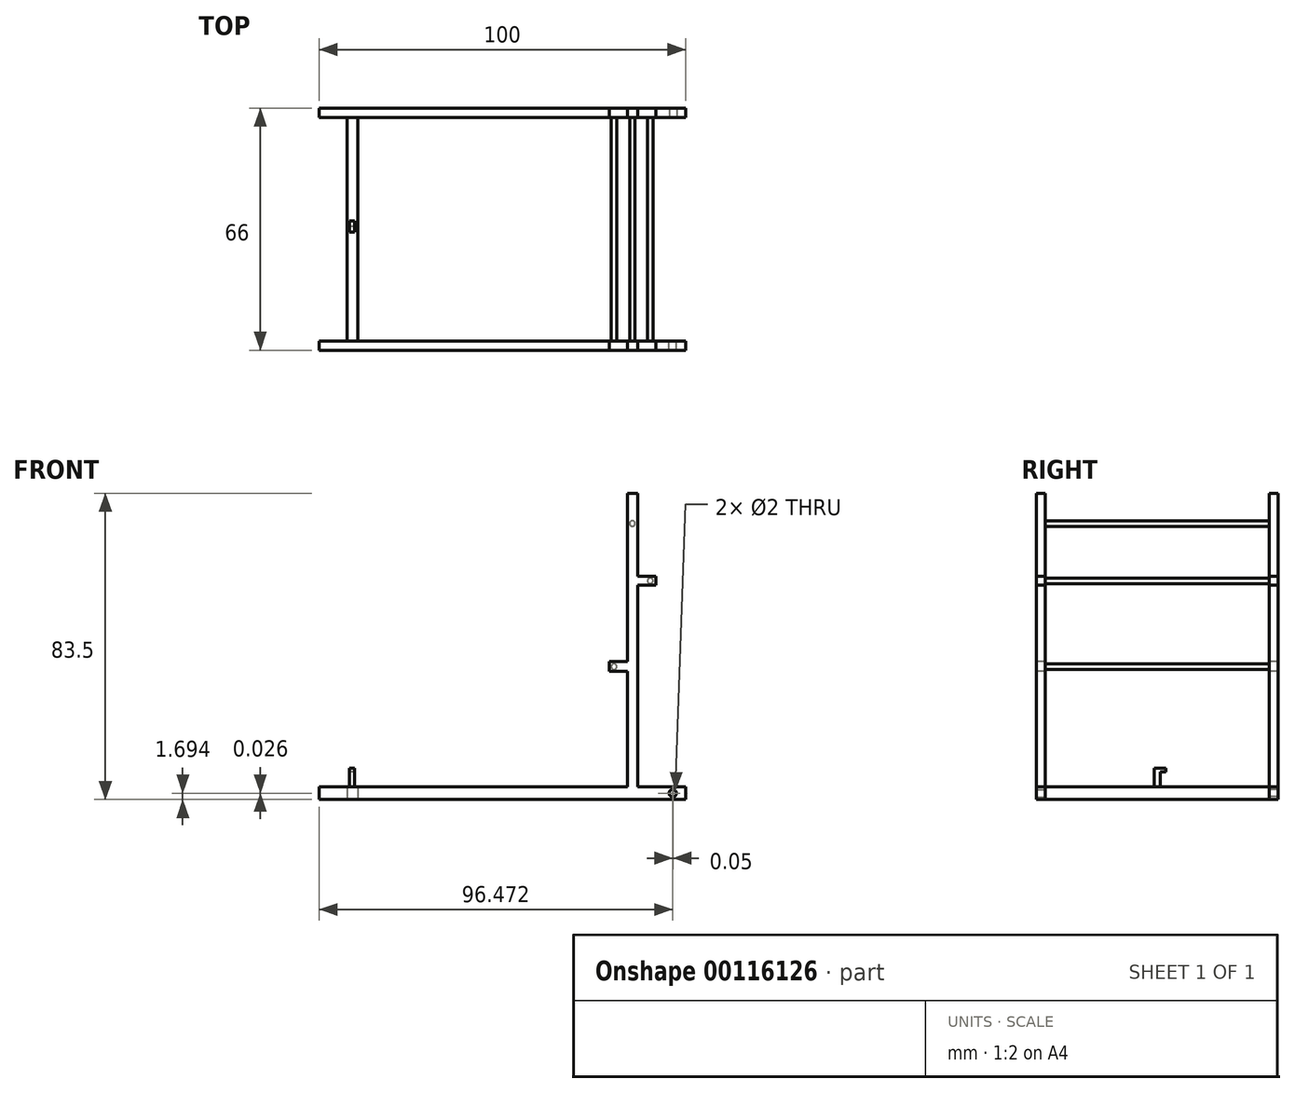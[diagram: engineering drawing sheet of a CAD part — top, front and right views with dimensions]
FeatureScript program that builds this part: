
annotation { "Feature Type Name" : "Feature", "Feature Type Description" : "" }
export const myFeature = defineFeature(function(context is Context, id is Id, definition is map)
    precondition{}
    {
        {
            var Q0;
            Q0=qCreatedBy(makeId("Front.planeOp"),FACE);
            var sketch = newSketch(context, id + "F0", { "sketchPlane" : qUnion([Q0])});
            skLineSegment(sketch, "E0", {"start": v(-48.3, 0) * mm, "end": v(51.7, 0) * mm});
            skLineSegment(sketch, "E1", {"start": v(-48.3, 0) * mm, "end": v(-48.3, 3.5) * mm});
            skLineSegment(sketch, "E2", {"start": v(-48.3, 3.5) * mm, "end": v(51.7, 3.5) * mm});
            skLineSegment(sketch, "E3", {"start": v(51.7, 3.5) * mm, "end": v(51.7, 0) * mm});
            skCircle(sketch, "E4", {"center": v(48.16, 1.7) * mm, "radius": 1 * mm});
            skSolve(sketch);
        }
        {
            var Q0;
            Q0=makeQuery(id+"F0.imprint","IMPRINT",FACE,{"disambiguationData":[TD([[makeQuery(id+"F0.imprint","IMPRINT",EDGE,{"derivedFrom":sQuery(id+"F0.wireOp",EDGE,"E0")}),1.0]])]});
            extrude(context, id + "F1", {"entities" : qUnion([Q0]), "depth" : 2.5 * mm});
        }
        {
            var Q0;
            Q0=qCreatedBy(makeId("Top.planeOp"),FACE);
            var sketch = newSketch(context, id + "F2", { "sketchPlane" : qUnion([Q0])});
            skLineSegment(sketch, "E5", {"start": v(0, 0) * mm, "end": v(0, 61) * mm});
            skSolve(sketch);
        }
        {
            var Q0;
            Q0=sQuery(id+"F2.wireOp",VERTEX,"E5.end");
            var Q1;
            Q1=qCreatedBy(makeId("Front.planeOp"),FACE);
            cPlane(context, id + "F3", {"entities" : qUnion([Q0, Q1]), "cplaneType" : CPlaneType.PLANE_POINT, "offset" : 25.4 * mm, "width" : 152.4 * mm, "height" : 152.4 * mm});
        }
        {
            var Q0;
            Q0=qCreatedBy(id+"F3.planeOp",FACE);
            var sketch = newSketch(context, id + "F4", { "sketchPlane" : qUnion([Q0])});
            skLineSegment(sketch, "E6", {"start": v(51.7, 0) * mm, "end": v(-48.3, 0) * mm});
            skLineSegment(sketch, "E7", {"start": v(51.7, 0) * mm, "end": v(51.7, 3.5) * mm});
            skLineSegment(sketch, "E8", {"start": v(51.7, 3.5) * mm, "end": v(-48.3, 3.5) * mm});
            skLineSegment(sketch, "E9", {"start": v(-48.3, 3.5) * mm, "end": v(-48.3, 0) * mm});
            skCircle(sketch, "E10", {"center": v(48.21, 1.72) * mm, "radius": 1 * mm});
            skSolve(sketch);
        }
        {
            var Q0;
            Q0=makeQuery(id+"F4.imprint","IMPRINT",FACE,{"disambiguationData":[TD([[makeQuery(id+"F4.imprint","IMPRINT",EDGE,{"derivedFrom":sQuery(id+"F4.wireOp",EDGE,"E6")}),-1.0]])]});
            extrude(context, id + "F5", {"entities" : qUnion([Q0]), "oppositeDirection" : true, "depth" : 2.5 * mm});
        }
        {
            var Q0;
            Q0=makeQuery(id+"F5.opExtrude","CAP_FACE",FACE,{"disambiguationData":[OSD([sQuery(id+"F4.wireOp",EDGE,"E6"),sQuery(id+"F4.wireOp",EDGE,"E7"),sQuery(id+"F4.wireOp",EDGE,"E8"),sQuery(id+"F4.wireOp",EDGE,"E9"),sQuery(id+"F4.wireOp",EDGE,"E10")])],"isStart":true});
            var sketch = newSketch(context, id + "F6", { "sketchPlane" : qUnion([Q0])});
            skLineSegment(sketch, "E11.bottom", {"start": v(-40.63, 3.5) * mm, "end": v(-37.73, 3.5) * mm});
            skLineSegment(sketch, "E11.top", {"start": v(-40.63, 0) * mm, "end": v(-37.73, 0) * mm});
            skLineSegment(sketch, "E11.left", {"start": v(-40.63, 3.5) * mm, "end": v(-40.63, 0) * mm});
            skLineSegment(sketch, "E11.right", {"start": v(-37.73, 3.5) * mm, "end": v(-37.73, 0) * mm});
            skSolve(sketch);
        }
        {
            var Q0;
            Q0=makeQuery(id+"F6.imprint","IMPRINT",FACE,{"disambiguationData":[TD([[makeQuery(id+"F6.imprint","IMPRINT",EDGE,{"derivedFrom":sQuery(id+"F6.wireOp",EDGE,"E11.bottom")}),1.0]])]});
            var Q1;
            Q1=makeQuery(id+"F1.opExtrude","CAP_FACE",FACE,{"disambiguationData":[OSD([sQuery(id+"F0.wireOp",EDGE,"E0"),sQuery(id+"F0.wireOp",EDGE,"E1"),sQuery(id+"F0.wireOp",EDGE,"E2"),sQuery(id+"F0.wireOp",EDGE,"E3"),sQuery(id+"F0.wireOp",EDGE,"E4")])],"isStart":true});
            extrude(context, id + "F7", {"entities" : qUnion([Q0]), "endBound" : BoundingType.UP_TO_SURFACE, "endBoundEntityFace" : qUnion([Q1]), "depth" : 25.4 * mm});
        }
        {
            var Q0;
            Q0=makeQuery(id+"F5.opExtrude","SWEPT_FACE",FACE,{"disambiguationData":[OSD([sQuery(id+"F4.wireOp",EDGE,"E8")])]});
            var sketch = newSketch(context, id + "F8", { "sketchPlane" : qUnion([Q0])});
            skLineSegment(sketch, "E12.bottom", {"start": v(35.83, 63.5) * mm, "end": v(38.55, 63.5) * mm});
            skLineSegment(sketch, "E12.top", {"start": v(35.83, 61) * mm, "end": v(38.55, 61) * mm});
            skLineSegment(sketch, "E12.left", {"start": v(35.83, 63.5) * mm, "end": v(35.83, 61) * mm});
            skLineSegment(sketch, "E12.right", {"start": v(38.55, 63.5) * mm, "end": v(38.55, 61) * mm});
            skLineSegment(sketch, "E13.bottom", {"start": v(38.55, 0) * mm, "end": v(35.83, 0) * mm});
            skLineSegment(sketch, "E13.top", {"start": v(38.55, -2.5) * mm, "end": v(35.83, -2.5) * mm});
            skLineSegment(sketch, "E13.left", {"start": v(38.55, 0) * mm, "end": v(38.55, -2.5) * mm});
            skLineSegment(sketch, "E13.right", {"start": v(35.83, 0) * mm, "end": v(35.83, -2.5) * mm});
            skSolve(sketch);
        }
        {
            var Q0;
            Q0=makeQuery(id+"F8.imprint","IMPRINT",FACE,{"disambiguationData":[TD([[makeQuery(id+"F8.imprint","IMPRINT",EDGE,{"derivedFrom":sQuery(id+"F8.wireOp",EDGE,"E13.bottom")}),1.0]])]});
            extrude(context, id + "F9", {"entities" : qUnion([Q0]), "operationType" : NewBodyOperationType.ADD, "depth" : 80 * mm});
        }
        {
            var Q0;
            Q0=makeQuery(id+"F8.imprint","IMPRINT",FACE,{"disambiguationData":[TD([[makeQuery(id+"F8.imprint","IMPRINT",EDGE,{"derivedFrom":sQuery(id+"F8.wireOp",EDGE,"E12.bottom")}),1.0]])]});
            extrude(context, id + "F10", {"entities" : qUnion([Q0]), "operationType" : NewBodyOperationType.ADD, "depth" : 80 * mm});
        }
        {
            var Q0;
            Q0=makeQuery(id+"F9.opExtrude","SWEPT_FACE",FACE,{"disambiguationData":[OSD([sQuery(id+"F8.wireOp",EDGE,"E13.left")])]});
            var sketch = newSketch(context, id + "F11", { "sketchPlane" : qUnion([Q0])});
            skLineSegment(sketch, "E14.bottom", {"start": v(-2.5, 60.8) * mm, "end": v(0, 60.8) * mm});
            skLineSegment(sketch, "E14.top", {"start": v(-2.5, 58.43) * mm, "end": v(0, 58.43) * mm});
            skLineSegment(sketch, "E14.left", {"start": v(-2.5, 60.8) * mm, "end": v(-2.5, 58.43) * mm});
            skLineSegment(sketch, "E14.right", {"start": v(0, 60.8) * mm, "end": v(0, 58.43) * mm});
            skSolve(sketch);
        }
        {
            var Q0;
            Q0=makeQuery(id+"F11.imprint","IMPRINT",FACE,{"disambiguationData":[TD([[makeQuery(id+"F11.imprint","IMPRINT",EDGE,{"derivedFrom":sQuery(id+"F11.wireOp",EDGE,"E14.bottom")}),-1.0]])]});
            extrude(context, id + "F12", {"entities" : qUnion([Q0]), "operationType" : NewBodyOperationType.ADD, "depth" : 5 * mm});
        }
        {
            var Q0;
            Q0=makeQuery(id+"F10.opExtrude","SWEPT_FACE",FACE,{"disambiguationData":[OSD([sQuery(id+"F8.wireOp",EDGE,"E12.right")])]});
            var sketch = newSketch(context, id + "F13", { "sketchPlane" : qUnion([Q0])});
            skLineSegment(sketch, "E15.bottom", {"start": v(61, 60.8) * mm, "end": v(63.5, 60.8) * mm});
            skLineSegment(sketch, "E15.top", {"start": v(61, 58.43) * mm, "end": v(63.5, 58.43) * mm});
            skLineSegment(sketch, "E15.left", {"start": v(61, 60.8) * mm, "end": v(61, 58.43) * mm});
            skLineSegment(sketch, "E15.right", {"start": v(63.5, 60.8) * mm, "end": v(63.5, 58.43) * mm});
            skSolve(sketch);
        }
        {
            var Q0;
            Q0=makeQuery(id+"F13.imprint","IMPRINT",FACE,{"disambiguationData":[TD([[makeQuery(id+"F13.imprint","IMPRINT",EDGE,{"derivedFrom":sQuery(id+"F13.wireOp",EDGE,"E15.bottom")}),-1.0]])]});
            extrude(context, id + "F14", {"entities" : qUnion([Q0]), "operationType" : NewBodyOperationType.ADD, "depth" : 5 * mm});
        }
        {
            var Q0;
            Q0=makeQuery(id+"F12.boolean.opBoolean","MERGE",FACE,{"derivedFrom":[makeQuery(id+"F9.boolean.opBoolean","MERGE",FACE,{"derivedFrom":[makeQuery(id+"F1.opExtrude","CAP_FACE",FACE,{"disambiguationData":[OSD([sQuery(id+"F0.wireOp",EDGE,"E0"),sQuery(id+"F0.wireOp",EDGE,"E1"),sQuery(id+"F0.wireOp",EDGE,"E2"),sQuery(id+"F0.wireOp",EDGE,"E3"),sQuery(id+"F0.wireOp",EDGE,"E4")])],"isStart":true}),makeQuery(id+"F9.opExtrude","SWEPT_FACE",FACE,{"disambiguationData":[OSD([sQuery(id+"F8.wireOp",EDGE,"E13.bottom")])]})]}),makeQuery(id+"F12.opExtrude","SWEPT_FACE",FACE,{"disambiguationData":[OSD([sQuery(id+"F11.wireOp",EDGE,"E14.right")])]})]});
            var sketch = newSketch(context, id + "F15", { "sketchPlane" : qUnion([Q0])});
            skCircle(sketch, "E16", {"center": v(-42.03, 59.62) * mm, "radius": 0.75 * mm});
            skPoint(sketch, "E16.centerSnap0", {"position": v(-43.55, 59.62) * mm});
            skSolve(sketch);
        }
        {
            var Q0;
            Q0=makeQuery(id+"F15.imprint","IMPRINT",FACE,{"disambiguationData":[TD([[makeQuery(id+"F15.imprint","IMPRINT",EDGE,{"derivedFrom":sQuery(id+"F15.wireOp",EDGE,"E16")}),1.0]])]});
            var Q1;
            Q1=makeQuery(id+"F14.boolean.opBoolean","MERGE",FACE,{"derivedFrom":[makeQuery(id+"F10.boolean.opBoolean","MERGE",FACE,{"derivedFrom":[makeQuery(id+"F5.opExtrude","CAP_FACE",FACE,{"disambiguationData":[OSD([sQuery(id+"F4.wireOp",EDGE,"E6"),sQuery(id+"F4.wireOp",EDGE,"E7"),sQuery(id+"F4.wireOp",EDGE,"E8"),sQuery(id+"F4.wireOp",EDGE,"E9"),sQuery(id+"F4.wireOp",EDGE,"E10")])],"isStart":true}),makeQuery(id+"F10.opExtrude","SWEPT_FACE",FACE,{"disambiguationData":[OSD([sQuery(id+"F8.wireOp",EDGE,"E12.top")])]})]}),makeQuery(id+"F14.opExtrude","SWEPT_FACE",FACE,{"disambiguationData":[OSD([sQuery(id+"F13.wireOp",EDGE,"E15.left")])]})]});
            extrude(context, id + "F16", {"entities" : qUnion([Q0]), "endBound" : BoundingType.UP_TO_SURFACE, "endBoundEntityFace" : qUnion([Q1]), "depth" : 25.4 * mm});
        }
        {
            var Q0;
            Q0=makeQuery(id+"F10.opExtrude","SWEPT_FACE",FACE,{"disambiguationData":[OSD([sQuery(id+"F8.wireOp",EDGE,"E12.left")])]});
            var sketch = newSketch(context, id + "F17", { "sketchPlane" : qUnion([Q0])});
            skLineSegment(sketch, "E17.bottom", {"start": v(-63.5, 37.67) * mm, "end": v(-61, 37.67) * mm});
            skLineSegment(sketch, "E17.top", {"start": v(-63.5, 34.88) * mm, "end": v(-61, 34.88) * mm});
            skLineSegment(sketch, "E17.left", {"start": v(-63.5, 37.67) * mm, "end": v(-63.5, 34.88) * mm});
            skLineSegment(sketch, "E17.right", {"start": v(-61, 37.67) * mm, "end": v(-61, 34.88) * mm});
            skSolve(sketch);
        }
        {
            var Q0;
            Q0=makeQuery(id+"F17.imprint","IMPRINT",FACE,{"disambiguationData":[TD([[makeQuery(id+"F17.imprint","IMPRINT",EDGE,{"derivedFrom":sQuery(id+"F17.wireOp",EDGE,"E17.bottom")}),-1.0]])]});
            extrude(context, id + "F18", {"entities" : qUnion([Q0]), "operationType" : NewBodyOperationType.ADD, "depth" : 5 * mm});
        }
        {
            var Q0;
            Q0=makeQuery(id+"F12.boolean.opBoolean","MERGE",FACE,{"derivedFrom":[makeQuery(id+"F9.boolean.opBoolean","MERGE",FACE,{"derivedFrom":[makeQuery(id+"F1.opExtrude","CAP_FACE",FACE,{"disambiguationData":[OSD([sQuery(id+"F0.wireOp",EDGE,"E0"),sQuery(id+"F0.wireOp",EDGE,"E1"),sQuery(id+"F0.wireOp",EDGE,"E2"),sQuery(id+"F0.wireOp",EDGE,"E3"),sQuery(id+"F0.wireOp",EDGE,"E4")])],"isStart":true}),makeQuery(id+"F9.opExtrude","SWEPT_FACE",FACE,{"disambiguationData":[OSD([sQuery(id+"F8.wireOp",EDGE,"E13.bottom")])]})]}),makeQuery(id+"F12.opExtrude","SWEPT_FACE",FACE,{"disambiguationData":[OSD([sQuery(id+"F11.wireOp",EDGE,"E14.right")])]})]});
            var sketch = newSketch(context, id + "F19", { "sketchPlane" : qUnion([Q0])});
            skCircle(sketch, "E18", {"center": v(-37.15, 75.23) * mm, "radius": 0.75 * mm});
            skSolve(sketch);
        }
        {
            var Q0;
            Q0=makeQuery(id+"F19.imprint","IMPRINT",FACE,{"disambiguationData":[TD([[makeQuery(id+"F19.imprint","IMPRINT",EDGE,{"derivedFrom":sQuery(id+"F19.wireOp",EDGE,"E18")}),1.0]])]});
            var Q1;
            Q1=makeQuery(id+"F18.boolean.opBoolean","MERGE",FACE,{"derivedFrom":[makeQuery(id+"F14.boolean.opBoolean","MERGE",FACE,{"derivedFrom":[makeQuery(id+"F10.boolean.opBoolean","MERGE",FACE,{"derivedFrom":[makeQuery(id+"F5.opExtrude","CAP_FACE",FACE,{"disambiguationData":[OSD([sQuery(id+"F4.wireOp",EDGE,"E6"),sQuery(id+"F4.wireOp",EDGE,"E7"),sQuery(id+"F4.wireOp",EDGE,"E8"),sQuery(id+"F4.wireOp",EDGE,"E9"),sQuery(id+"F4.wireOp",EDGE,"E10")])],"isStart":true}),makeQuery(id+"F10.opExtrude","SWEPT_FACE",FACE,{"disambiguationData":[OSD([sQuery(id+"F8.wireOp",EDGE,"E12.top")])]})]}),makeQuery(id+"F14.opExtrude","SWEPT_FACE",FACE,{"disambiguationData":[OSD([sQuery(id+"F13.wireOp",EDGE,"E15.left")])]})]}),makeQuery(id+"F18.opExtrude","SWEPT_FACE",FACE,{"disambiguationData":[OSD([sQuery(id+"F17.wireOp",EDGE,"E17.right")])]})]});
            extrude(context, id + "F20", {"entities" : qUnion([Q0]), "endBound" : BoundingType.UP_TO_SURFACE, "endBoundEntityFace" : qUnion([Q1]), "depth" : 25.4 * mm});
        }
        {
            var Q0;
            Q0=makeQuery(id+"F9.opExtrude","SWEPT_FACE",FACE,{"disambiguationData":[OSD([sQuery(id+"F8.wireOp",EDGE,"E13.right")])]});
            var sketch = newSketch(context, id + "F21", { "sketchPlane" : qUnion([Q0])});
            skLineSegment(sketch, "E19.bottom", {"start": v(0, 37.67) * mm, "end": v(2.5, 37.67) * mm});
            skLineSegment(sketch, "E19.top", {"start": v(0, 34.88) * mm, "end": v(2.5, 34.88) * mm});
            skLineSegment(sketch, "E19.left", {"start": v(0, 37.67) * mm, "end": v(0, 34.88) * mm});
            skLineSegment(sketch, "E19.right", {"start": v(2.5, 37.67) * mm, "end": v(2.5, 34.88) * mm});
            skSolve(sketch);
        }
        {
            var Q0;
            Q0=makeQuery(id+"F21.imprint","IMPRINT",FACE,{"disambiguationData":[TD([[makeQuery(id+"F21.imprint","IMPRINT",EDGE,{"derivedFrom":sQuery(id+"F21.wireOp",EDGE,"E19.bottom")}),-1.0]])]});
            extrude(context, id + "F22", {"entities" : qUnion([Q0]), "operationType" : NewBodyOperationType.ADD, "depth" : 5 * mm});
        }
        {
            var Q0;
            Q0=makeQuery(id+"F22.boolean.opBoolean","MERGE",FACE,{"derivedFrom":[makeQuery(id+"F12.boolean.opBoolean","MERGE",FACE,{"derivedFrom":[makeQuery(id+"F9.boolean.opBoolean","MERGE",FACE,{"derivedFrom":[makeQuery(id+"F1.opExtrude","CAP_FACE",FACE,{"disambiguationData":[OSD([sQuery(id+"F0.wireOp",EDGE,"E0"),sQuery(id+"F0.wireOp",EDGE,"E1"),sQuery(id+"F0.wireOp",EDGE,"E2"),sQuery(id+"F0.wireOp",EDGE,"E3"),sQuery(id+"F0.wireOp",EDGE,"E4")])],"isStart":true}),makeQuery(id+"F9.opExtrude","SWEPT_FACE",FACE,{"disambiguationData":[OSD([sQuery(id+"F8.wireOp",EDGE,"E13.bottom")])]})]}),makeQuery(id+"F12.opExtrude","SWEPT_FACE",FACE,{"disambiguationData":[OSD([sQuery(id+"F11.wireOp",EDGE,"E14.right")])]})]}),makeQuery(id+"F22.opExtrude","SWEPT_FACE",FACE,{"disambiguationData":[OSD([sQuery(id+"F21.wireOp",EDGE,"E19.left")])]})]});
            var sketch = newSketch(context, id + "F23", { "sketchPlane" : qUnion([Q0])});
            skCircle(sketch, "E20", {"center": v(-32.15, 36.2) * mm, "radius": 0.75 * mm});
            skSolve(sketch);
        }
        {
            var Q0;
            Q0=makeQuery(id+"F23.imprint","IMPRINT",FACE,{"disambiguationData":[TD([[makeQuery(id+"F23.imprint","IMPRINT",EDGE,{"derivedFrom":sQuery(id+"F23.wireOp",EDGE,"E20")}),1.0]])]});
            var Q1;
            Q1=makeQuery(id+"F18.boolean.opBoolean","MERGE",FACE,{"derivedFrom":[makeQuery(id+"F14.boolean.opBoolean","MERGE",FACE,{"derivedFrom":[makeQuery(id+"F10.boolean.opBoolean","MERGE",FACE,{"derivedFrom":[makeQuery(id+"F5.opExtrude","CAP_FACE",FACE,{"disambiguationData":[OSD([sQuery(id+"F4.wireOp",EDGE,"E6"),sQuery(id+"F4.wireOp",EDGE,"E7"),sQuery(id+"F4.wireOp",EDGE,"E8"),sQuery(id+"F4.wireOp",EDGE,"E9"),sQuery(id+"F4.wireOp",EDGE,"E10")])],"isStart":true}),makeQuery(id+"F10.opExtrude","SWEPT_FACE",FACE,{"disambiguationData":[OSD([sQuery(id+"F8.wireOp",EDGE,"E12.top")])]})]}),makeQuery(id+"F14.opExtrude","SWEPT_FACE",FACE,{"disambiguationData":[OSD([sQuery(id+"F13.wireOp",EDGE,"E15.left")])]})]}),makeQuery(id+"F18.opExtrude","SWEPT_FACE",FACE,{"disambiguationData":[OSD([sQuery(id+"F17.wireOp",EDGE,"E17.right")])]})]});
            extrude(context, id + "F24", {"entities" : qUnion([Q0]), "endBound" : BoundingType.UP_TO_SURFACE, "endBoundEntityFace" : qUnion([Q1]), "depth" : 25.4 * mm});
        }
        {
            var Q0;
            Q0=makeQuery(id+"F7.opExtrude","SWEPT_FACE",FACE,{"disambiguationData":[OSD([sQuery(id+"F6.wireOp",EDGE,"E11.bottom")])]});
            var sketch = newSketch(context, id + "F25", { "sketchPlane" : qUnion([Q0])});
            skLineSegment(sketch, "E21.bottom", {"start": v(-38.66, 31.28) * mm, "end": v(-40.06, 31.28) * mm});
            skLineSegment(sketch, "E21.top", {"start": v(-38.66, 29.72) * mm, "end": v(-40.06, 29.72) * mm});
            skLineSegment(sketch, "E21.left", {"start": v(-38.66, 31.28) * mm, "end": v(-38.66, 29.72) * mm});
            skLineSegment(sketch, "E21.right", {"start": v(-40.06, 31.28) * mm, "end": v(-40.06, 29.72) * mm});
            skSolve(sketch);
        }
        {
            var Q0;
            Q0=makeQuery(id+"F25.imprint","IMPRINT",FACE,{"disambiguationData":[TD([[makeQuery(id+"F25.imprint","IMPRINT",EDGE,{"derivedFrom":sQuery(id+"F25.wireOp",EDGE,"E21.bottom")}),1.0]])]});
            extrude(context, id + "F26", {"entities" : qUnion([Q0]), "operationType" : NewBodyOperationType.ADD, "depth" : 5 * mm});
        }
        {
            var Q0;
            Q0=makeQuery(id+"F26.opExtrude","SWEPT_FACE",FACE,{"disambiguationData":[OSD([sQuery(id+"F25.wireOp",EDGE,"E21.bottom")])]});
            var sketch = newSketch(context, id + "F27", { "sketchPlane" : qUnion([Q0])});
            skLineSegment(sketch, "E22.bottom", {"start": v(38.66, 8.5) * mm, "end": v(40.06, 8.5) * mm});
            skLineSegment(sketch, "E22.top", {"start": v(38.66, 7.48) * mm, "end": v(40.06, 7.48) * mm});
            skLineSegment(sketch, "E22.left", {"start": v(38.66, 8.5) * mm, "end": v(38.66, 7.48) * mm});
            skLineSegment(sketch, "E22.right", {"start": v(40.06, 8.5) * mm, "end": v(40.06, 7.48) * mm});
            skSolve(sketch);
        }
        {
            var Q0;
            Q0=makeQuery(id+"F27.imprint","IMPRINT",FACE,{"disambiguationData":[TD([[makeQuery(id+"F27.imprint","IMPRINT",EDGE,{"derivedFrom":sQuery(id+"F27.wireOp",EDGE,"E22.bottom")}),-1.0]])]});
            extrude(context, id + "F28", {"entities" : qUnion([Q0]), "operationType" : NewBodyOperationType.ADD, "depth" : 1.5 * mm});
        }
    });
